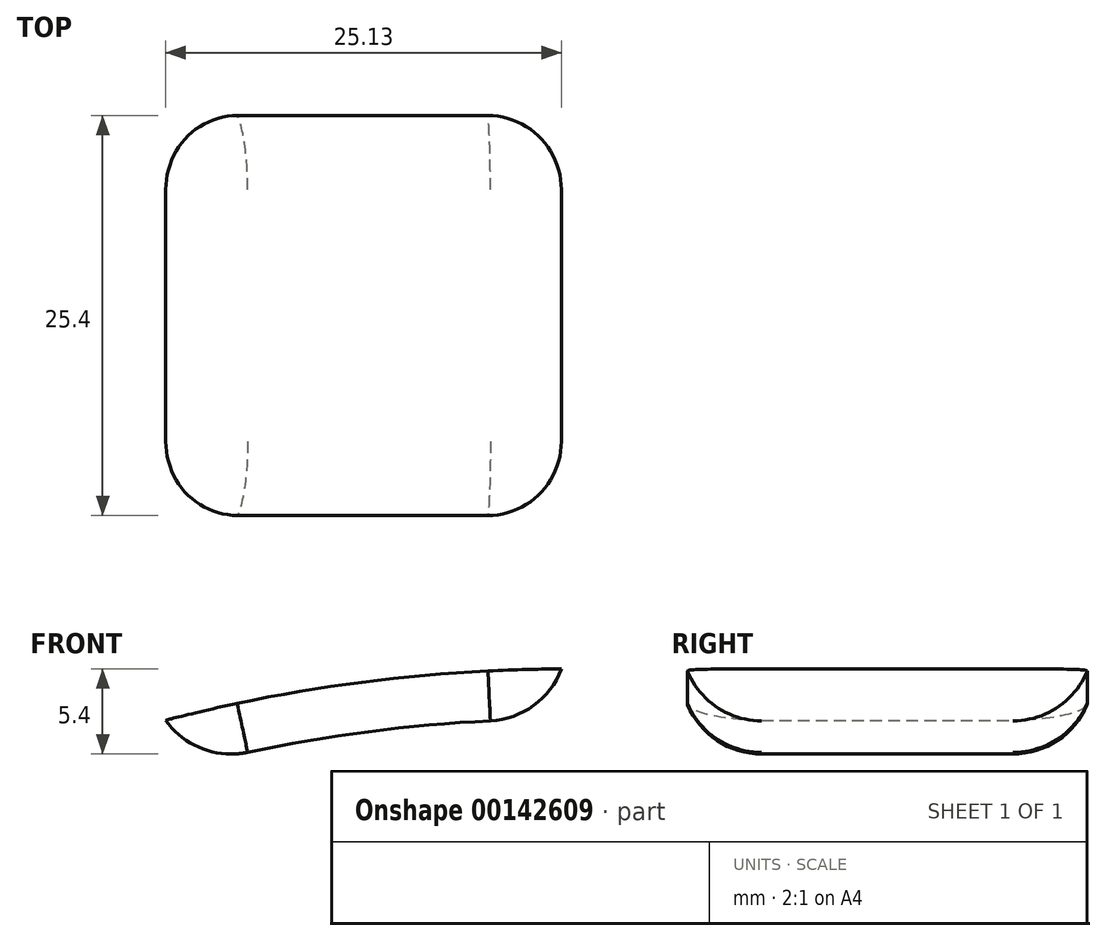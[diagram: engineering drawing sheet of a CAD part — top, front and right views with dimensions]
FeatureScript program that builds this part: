
annotation { "Feature Type Name" : "Feature", "Feature Type Description" : "" }
export const myFeature = defineFeature(function(context is Context, id is Id, definition is map)
    precondition{}
    {
        {
            var Q0;
            Q0=qCreatedBy(makeId("Front.planeOp"),FACE);
            var sketch = newSketch(context, id + "F0", { "sketchPlane" : qUnion([Q0])});
            skArc(sketch, "E0", {"start": v(-0.4, 101.6) * mm, "mid": v(-13.06, 100.76) * mm, "end": v(-25.52, 98.34) * mm});
            skArc(sketch, "E1", {"start": v(-0.38, 98.42) * mm, "mid": v(-12.65, 97.6) * mm, "end": v(-24.72, 95.27) * mm});
            skLineSegment(sketch, "E2", {"start": v(-24.72, 95.27) * mm, "end": v(-27.08, 104.38) * mm});
            skLineSegment(sketch, "E3", {"start": v(-0.38, 98.42) * mm, "end": v(-0.43, 112.33) * mm});
            skSolve(sketch);
        }
        {
            var Q0;
            {var subQ0=sQuery(id+"F0.wireOp",EDGE,"E0");Q0=makeQuery(id+"F0.imprint","IMPRINT",FACE,{"disambiguationData":[TD([[makeQuery(id+"F0.imprint","IMPRINT",EDGE,{"derivedFrom":subQ0}),1.0]])]});}
            extrude(context, id + "F1", {"entities" : qUnion([Q0]), "depth" : 25.4 * mm});
        }
        {
            var Q0;
            Q0=makeQuery(id+"F1.opExtrude","CAP_EDGE",EDGE,{"disambiguationData":[OSD([sQuery(id+"F0.wireOp",EDGE,"E1")])],"isStart":false});
            var Q1;
            Q1=makeQuery(id+"F1.opExtrude","SWEPT_EDGE",EDGE,{"disambiguationData":[OSD([sQuery(id+"F0.wireOp",EDGE,"E1"),sQuery(id+"F0.wireOp",EDGE,"E2")])]});
            var Q2;
            Q2=makeQuery(id+"F1.opExtrude","CAP_EDGE",EDGE,{"disambiguationData":[OSD([sQuery(id+"F0.wireOp",EDGE,"E1")])],"isStart":true});
            var Q3;
            Q3=makeQuery(id+"F1.opExtrude","SWEPT_EDGE",EDGE,{"disambiguationData":[OSD([sQuery(id+"F0.wireOp",EDGE,"E1"),sQuery(id+"F0.wireOp",EDGE,"E3")])]});
            fillet(context, id + "F2", {"entities" : qUnion([Q0, Q1, Q2, Q3]), "radius" : 5.08 * mm, "tangentPropagation" : true, "allowEdgeOverflow" : false});
        }
        {
            var Q0;
            {var subQ0=sQuery(id+"F0.wireOp",EDGE,"E1");Q0=makeQuery(id+"F2.opFillet","BLEND_EDGE",EDGE,{"blendedFrom":[makeQuery(id+"F1.opExtrude","SWEPT_EDGE",EDGE,{"disambiguationData":[OSD([subQ0,sQuery(id+"F0.wireOp",EDGE,"E2")])]}),makeQuery(id+"F1.opExtrude","CAP_EDGE",EDGE,{"disambiguationData":[OSD([subQ0])],"isStart":false})],"blendedInto":[]});}
            var Q1;
            {var subQ0=sQuery(id+"F0.wireOp",EDGE,"E1");Q1=makeQuery(id+"F2.opFillet","BLEND_EDGE",EDGE,{"blendedFrom":[makeQuery(id+"F1.opExtrude","SWEPT_EDGE",EDGE,{"disambiguationData":[OSD([subQ0,sQuery(id+"F0.wireOp",EDGE,"E3")])]}),makeQuery(id+"F1.opExtrude","CAP_EDGE",EDGE,{"disambiguationData":[OSD([subQ0])],"isStart":false})],"blendedInto":[]});}
            var Q2;
            {var subQ0=sQuery(id+"F0.wireOp",EDGE,"E1");Q2=makeQuery(id+"F2.opFillet","BLEND_EDGE",EDGE,{"blendedFrom":[makeQuery(id+"F1.opExtrude","SWEPT_EDGE",EDGE,{"disambiguationData":[OSD([subQ0,sQuery(id+"F0.wireOp",EDGE,"E3")])]}),makeQuery(id+"F1.opExtrude","CAP_EDGE",EDGE,{"disambiguationData":[OSD([subQ0])],"isStart":true})],"blendedInto":[]});}
            var Q3;
            {var subQ0=sQuery(id+"F0.wireOp",EDGE,"E1");Q3=makeQuery(id+"F2.opFillet","BLEND_EDGE",EDGE,{"blendedFrom":[makeQuery(id+"F1.opExtrude","SWEPT_EDGE",EDGE,{"disambiguationData":[OSD([subQ0,sQuery(id+"F0.wireOp",EDGE,"E2")])]}),makeQuery(id+"F1.opExtrude","CAP_EDGE",EDGE,{"disambiguationData":[OSD([subQ0])],"isStart":true})],"blendedInto":[]});}
            fillet(context, id + "F3", {"entities" : qUnion([Q0, Q1, Q2, Q3]), "radius" : 5.08 * mm, "tangentPropagation" : true, "allowEdgeOverflow" : false});
        }
    });
